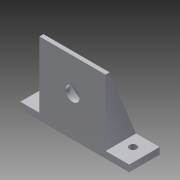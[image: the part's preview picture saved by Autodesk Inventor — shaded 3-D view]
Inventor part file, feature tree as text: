
AUTODESK INVENTOR PART (.ipt)
format: ipt  version: 2014 SP1 (Build 180222100, 222)  size: 150,016 bytes
history: native  units: mm
features: extrude x6, sketch x6
ambient origin geometry x8: Origin, YZ Plane, XZ Plane, XY Plane, X Axis, Y Axis, Z Axis, Center Point
bodies: Body1 (feature_tree)
feature tree (12):
  extrude  "Extrusion5"  Depth=20.0mm
  extrude  "Extrusion6"  Depth=10.0mm
  extrude  "Extrusion7"  Depth=5.5mm
  extrude  "Extrusion8"  Depth=50.0mm
  extrude  "Extrusion9"  Depth=3.0mm TaperAngle=0.0deg
  extrude  "Extrusion10"  Depth=3.0mm TaperAngle=0.0deg
  sketch  "Sketch6"  dims[d32=82.3mm d33=20.0mm]
  sketch  "Sketch7"  dims[d34=10.0mm d35=10.0mm]
  sketch  "Sketch8"  dims[d36=5.5mm d37=5.5mm]
  sketch  "Sketch9"  dims[d38=5.0mm d39=0.0mm d40=50.0mm]
  sketch  "Sketch10"  dims[d41=50.0mm d42=3.0mm d43=0.0mm]
  sketch  "Sketch11"  dims[d44=3.0mm d45=0.0mm d46=3.0mm d47=0.0mm d48=22.5mm d49=24.5mm d50=7.0mm d51=0.0mm d52=10.8mm d53=7.0mm d54=0.0mm]
